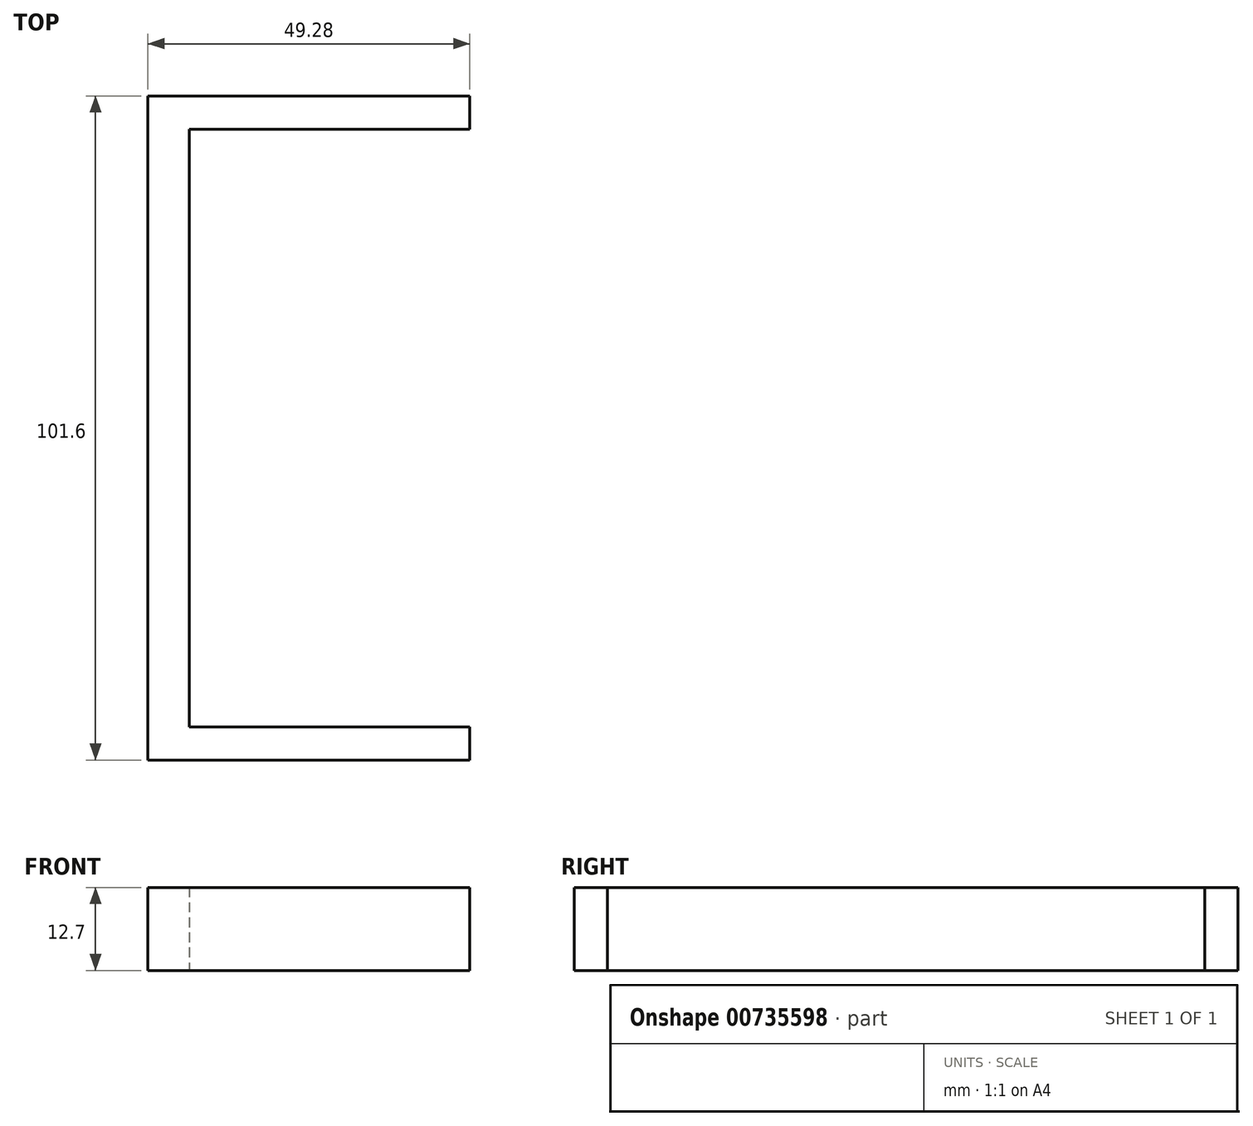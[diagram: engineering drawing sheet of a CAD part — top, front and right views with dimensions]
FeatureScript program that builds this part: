
annotation { "Feature Type Name" : "Feature", "Feature Type Description" : "" }
export const myFeature = defineFeature(function(context is Context, id is Id, definition is map)
    precondition{}
    {
        {
            var Q0;
            Q0=qCreatedBy(makeId("Top.planeOp"),FACE);
            var sketch = newSketch(context, id + "F0", { "sketchPlane" : qUnion([Q0])});
            skLineSegment(sketch, "E0", {"start": v(-28.71, 34.43) * mm, "end": v(-46.94, -53.48) * mm});
            skArc(sketch, "E1", {"start": v(44.65, 34.43) * mm, "mid": v(7.97, 59.21) * mm, "end": v(-28.71, 34.43) * mm});
            skLineSegment(sketch, "E2", {"start": v(44.65, 34.43) * mm, "end": v(65.4, -54.08) * mm});
            skLineSegment(sketch, "E3", {"start": v(-46.94, -53.48) * mm, "end": v(65.4, -54.08) * mm});
            skSolve(sketch);
        }
        {
            var Q0;
            Q0=makeQuery(id+"F0.imprint","IMPRINT",FACE,{"disambiguationData":[TD([[makeQuery(id+"F0.imprint","IMPRINT",EDGE,{"derivedFrom":sQuery(id+"F0.wireOp",EDGE,"E0")}),1.0]])]});
            extrude(context, id + "F1", {"entities" : qUnion([Q0]), "depth" : 45.72 * mm, "offsetDistance" : 25.4 * mm});
        }
        {
            var Q0;
            Q0=makeQuery(id+"F1.opExtrude","CAP_FACE",FACE,{"disambiguationData":[OSD([sQuery(id+"F0.wireOp",EDGE,"E0"),sQuery(id+"F0.wireOp",EDGE,"E1"),sQuery(id+"F0.wireOp",EDGE,"E2"),sQuery(id+"F0.wireOp",EDGE,"E3")])],"isStart":false});
            extrude(context, id + "F2", {"entities" : qUnion([Q0]), "operationType" : NewBodyOperationType.REMOVE, "oppositeDirection" : true, "depth" : 3.17 * mm, "offsetDistance" : 25.4 * mm});
        }
        {
            var Q0;
            Q0=makeQuery(id+"F2.boolean.opBoolean","COPY",FACE,{"derivedFrom":makeQuery(id+"F2.opExtrude","CAP_FACE",FACE,{"disambiguationData":[OSD([sQuery(id+"F0.wireOp",EDGE,"E0"),sQuery(id+"F0.wireOp",EDGE,"E1"),sQuery(id+"F0.wireOp",EDGE,"E2"),sQuery(id+"F0.wireOp",EDGE,"E3")])],"isStart":false})});
            extrude(context, id + "F3", {"entities" : qUnion([Q0]), "operationType" : NewBodyOperationType.REMOVE, "oppositeDirection" : true, "depth" : 25.4 * mm, "offsetDistance" : 25.4 * mm});
        }
        {
            var Q0;
            Q0=makeQuery(id+"F3.boolean.opBoolean","COPY",FACE,{"derivedFrom":makeQuery(id+"F3.opExtrude","CAP_FACE",FACE,{"disambiguationData":[OSD([sQuery(id+"F0.wireOp",EDGE,"E0"),sQuery(id+"F0.wireOp",EDGE,"E1"),sQuery(id+"F0.wireOp",EDGE,"E2"),sQuery(id+"F0.wireOp",EDGE,"E3")])],"isStart":false})});
            extrude(context, id + "F4", {"entities" : qUnion([Q0]), "operationType" : NewBodyOperationType.REMOVE, "endBound" : BoundingType.THROUGH_ALL, "oppositeDirection" : true, "depth" : 25.4 * mm, "offsetDistance" : 25.4 * mm});
        }
        {
            var Q0;
            Q0=qCreatedBy(makeId("Right.planeOp"),FACE);
            var sketch = newSketch(context, id + "F5", { "sketchPlane" : qUnion([Q0])});
            skLineSegment(sketch, "E4.bottom", {"start": v(-53.32, 20.67) * mm, "end": v(48.28, 20.67) * mm});
            skLineSegment(sketch, "E4.top", {"start": v(-53.32, 7.97) * mm, "end": v(48.28, 7.97) * mm});
            skLineSegment(sketch, "E4.left", {"start": v(-53.32, 20.67) * mm, "end": v(-53.32, 7.97) * mm});
            skLineSegment(sketch, "E4.right", {"start": v(48.28, 20.67) * mm, "end": v(48.28, 7.97) * mm});
            skSolve(sketch);
        }
        {
            var Q0;
            Q0 = qSketchRegion(id + "F5", true);
            extrude(context, id + "F6", {"entities" : qUnion([Q0]), "depth" : 6.35 * mm, "offsetDistance" : 25.4 * mm});
        }
        {
            var Q0;
            Q0=makeQuery(id+"F6.opExtrude","CAP_FACE",FACE,{"disambiguationData":[OSD([sQuery(id+"F5.wireOp",EDGE,"E4.bottom"),sQuery(id+"F5.wireOp",EDGE,"E4.top"),sQuery(id+"F5.wireOp",EDGE,"E4.left"),sQuery(id+"F5.wireOp",EDGE,"E4.right")])],"isStart":false});
            var sketch = newSketch(context, id + "F7", { "sketchPlane" : qUnion([Q0])});
            skLineSegment(sketch, "E5.bottom", {"start": v(-53.32, 20.67) * mm, "end": v(-48.24, 20.67) * mm});
            skLineSegment(sketch, "E5.top", {"start": v(-53.32, 7.97) * mm, "end": v(-48.24, 7.97) * mm});
            skLineSegment(sketch, "E5.left", {"start": v(-53.32, 20.67) * mm, "end": v(-53.32, 7.97) * mm});
            skLineSegment(sketch, "E5.right", {"start": v(-48.24, 20.67) * mm, "end": v(-48.24, 7.97) * mm});
            skLineSegment(sketch, "E6.bottom", {"start": v(48.28, 20.67) * mm, "end": v(43.2, 20.67) * mm});
            skLineSegment(sketch, "E6.top", {"start": v(48.28, 7.97) * mm, "end": v(43.2, 7.97) * mm});
            skLineSegment(sketch, "E6.left", {"start": v(48.28, 20.67) * mm, "end": v(48.28, 7.97) * mm});
            skLineSegment(sketch, "E6.right", {"start": v(43.2, 20.67) * mm, "end": v(43.2, 7.97) * mm});
            skSolve(sketch);
        }
        {
            var Q0;
            Q0=makeQuery(id+"F7.imprint","IMPRINT",FACE,{"disambiguationData":[TD([[makeQuery(id+"F7.imprint","IMPRINT",EDGE,{"derivedFrom":sQuery(id+"F7.wireOp",EDGE,"E5.bottom")}),-1.0]])]});
            var Q1;
            Q1=makeQuery(id+"F7.imprint","IMPRINT",FACE,{"disambiguationData":[TD([[makeQuery(id+"F7.imprint","IMPRINT",EDGE,{"derivedFrom":sQuery(id+"F7.wireOp",EDGE,"E6.bottom")}),-1.0]])]});
            extrude(context, id + "F8", {"entities" : qUnion([Q0, Q1]), "operationType" : NewBodyOperationType.ADD, "depth" : 42.93 * mm, "offsetDistance" : 25.4 * mm});
        }
    });
